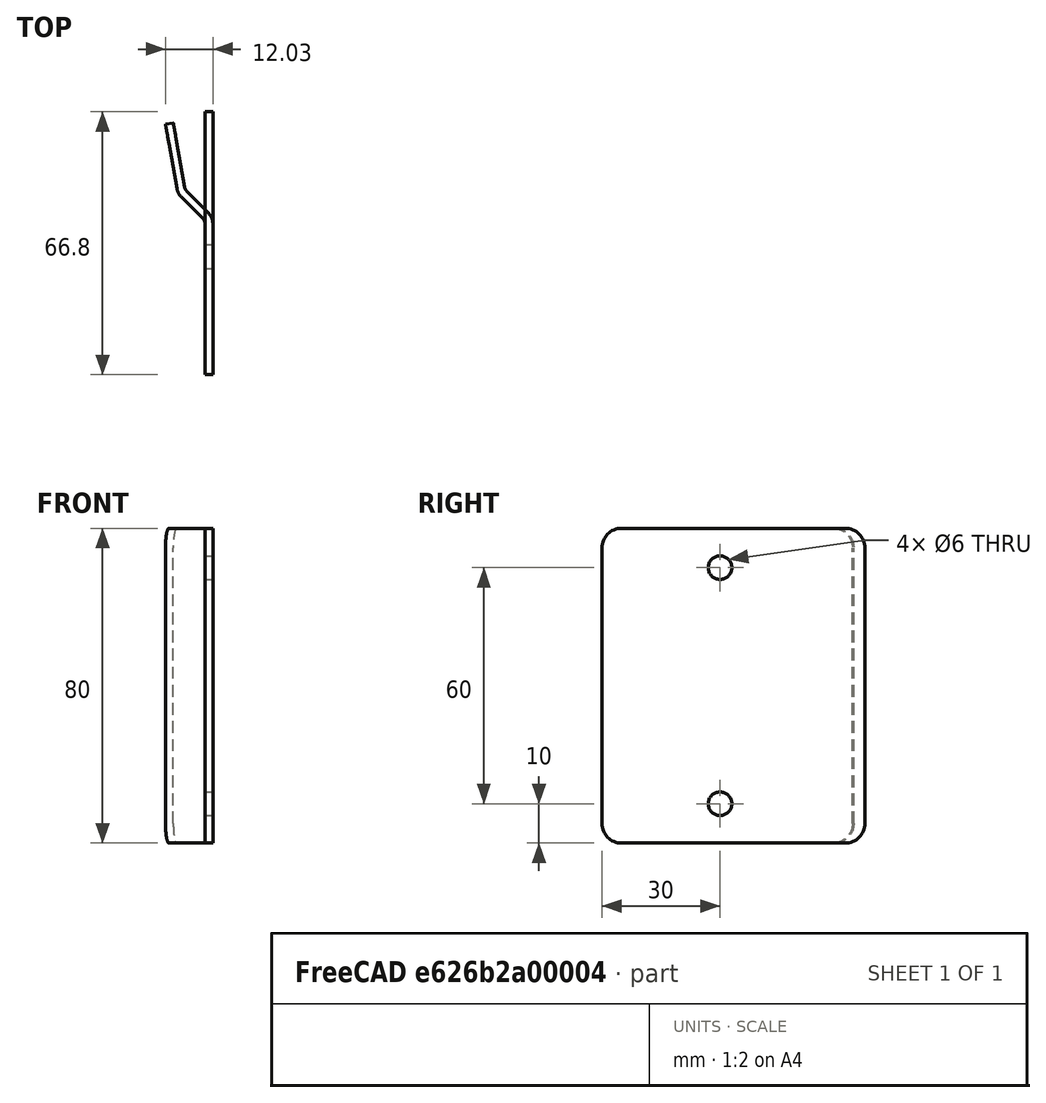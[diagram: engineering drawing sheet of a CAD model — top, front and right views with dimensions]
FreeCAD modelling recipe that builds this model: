
FCSTD DOCUMENT  (FreeCAD 0.22R37100 (Git))
Label: wall_mounted_stand_fix
License: All rights reserved
LicenseURL: http://en.wikipedia.org/wiki/All_rights_reserved
objects: Sketcher::SketchObject×8, TechDraw::DrawViewDimension×8, PartDesign::Pocket×3, TechDraw::DrawViewPart×3, App::DocumentObjectGroup×2, PartDesign::SubShapeBinder×1, PartDesign::FeaturePython×1, PartDesign::Mirrored×1, PartDesign::Body×1, TechDraw::DrawSVGTemplate×1, Part::Feature×1, TechDraw::DrawPage×1
note: 35 computed .brp shape members not serialized (recipe doc carries the construction recipe); baked Part::Feature solids carry a one-line shape summary decoded from their .brp

FEATURE [Sketcher::SketchObject] Sketch
  FullyConstrained = true
  sketch-geometry (3):
    g0: LineSegment StartX=0 StartY=0 StartZ=0 EndX=0 EndY=40 EndZ=0
    g1: LineSegment StartX=0 StartY=40 StartZ=0 EndX=-7.07107 EndY=47.0711 EndZ=0
    g2: LineSegment StartX=-7.07107 StartY=47.0711 StartZ=0 EndX=-10.0561 EndY=64 EndZ=0
  constraints (10):
    c: Coincident(g-1,g0)
    c: PointOnObject(g0,g-2)
    c: Coincident(g0,g1)
    c: Coincident(g1,g2)
    c: Angle(g1,g0) = 2.35619
    c: Angle(g1,g2) = 2.53073
    c: DistanceY(g0,g0) = 40
    c: Distance(g1) = 10
    c: Distance(g2) = 17.1901
    c: DistanceY(g0,g2) = 24
FEATURE [PartDesign::SubShapeBinder] Binder
  BindCopyOnChange = 0
  BindMode = 0
  ClaimChildren = true
  Context = -> Body [Binder.]
  Fuse = false
  MakeFace = true
  OffsetFill = false
  OffsetIntersection = false
  OffsetJoinType = 0
  OffsetOpenResult = false
  PartialLoad = false
  Relative = false
  Support = -> [Sketch]
  _Version = 2
FEATURE [PartDesign::FeaturePython] BaseBend  # WARN: FeaturePython — macro-defined, semantics opaque (R4)
  BendSide = 1
  BendSketch = -> Binder
  MidPlane = true
  Reverse = false
  Suppressed = false
  length = 80
  radius = 2
  thickness = 2
FEATURE [Sketcher::SketchObject] Sketch001
  AttachmentSupport = -> [YZ_Plane]
  FullyConstrained = true
  MapMode = 5
  Placement = pos=(0,0,0) rot=(0.57735,0.57735,0.57735;2.0944rad)
  sketch-geometry (2):
    g0: Circle CenterX=30 CenterY=30 CenterZ=0 NormalX=0 NormalY=0 NormalZ=1 AngleXU=0 Radius=3
    g1: Circle CenterX=30 CenterY=-30 CenterZ=0 NormalX=0 NormalY=0 NormalZ=1 AngleXU=0 Radius=3
  constraints (5):
    c: Symmetric(g1,g0,g-1)
    c: Equal(g0,g1)
    c: Diameter(g0) = 6
    c: DistanceX(g0) = 30
    c: DistanceY(g0) = 30
FEATURE [PartDesign::Pocket] Pocket
  BaseFeature = -> BaseBend
  Direction = (-1,0,0)
  Length = 5
  Length2 = 5
  Midplane = true
  Profile = -> Sketch001
  ReferenceAxis = -> Sketch001 [N_Axis]
  Suppressed = false
  Type = 1
FEATURE [Sketcher::SketchObject] Sketch003
  AttachmentOffset = pos=(0,40,0) rot=(0,0,1;0rad)
  AttachmentSupport = -> [YZ_Plane]
  FullyConstrained = true
  MapMode = 5
  Placement = pos=(0,0,40) rot=(0.57735,0.57735,0.57735;2.0944rad)
  expr: .AttachmentOffset.Base.y = <<BaseBend>>.length / 2
  sketch-geometry (3):
    g0: ArcOfCircle CenterX=5 CenterY=-5 CenterZ=0 NormalX=0 NormalY=0 NormalZ=1 AngleXU=0 Radius=5 StartAngle=1.5708 EndAngle=3.14159
    g1: LineSegment StartX=0 StartY=-5 StartZ=0 EndX=0 EndY=0 EndZ=0
    g2: LineSegment StartX=0 StartY=0 StartZ=0 EndX=5 EndY=0 EndZ=0
  constraints (7):
    c: Tangent(g0,g-1) = 1.5708
    c: Tangent(g0,g-2) = 1.5708
    c: Coincident(g0,g1)
    c: Coincident(g1,g2)
    c: Radius(g0) = 5
    c: Coincident(g2,g0)
    c: Coincident(g1,g-1)
FEATURE [Sketcher::SketchObject] Sketch004
  AttachmentOffset = pos=(0,40,0) rot=(0,-1,0;1.5708rad)
  AttachmentSupport = -> [Binder]
  FullyConstrained = true
  MapMode = 7
  Placement = pos=(-10.0561,64,40) rot=(0.6444,-0.540716,-0.540716;1.99673rad)
  expr: .AttachmentOffset.Base.y = <<BaseBend>>.length / 2
  sketch-geometry (3):
    g0: LineSegment StartX=3.14895e-11 StartY=-3.14335e-11 StartZ=0 EndX=5.00002 EndY=-3.14335e-11 EndZ=0
    g1: LineSegment StartX=3.14895e-11 StartY=-5.00002 StartZ=0 EndX=3.14895e-11 EndY=-3.14335e-11 EndZ=0
    g2: ArcOfCircle CenterX=5 CenterY=-5 CenterZ=0 NormalX=0 NormalY=0 NormalZ=1 AngleXU=0 Radius=5 StartAngle=1.57079 EndAngle=3.1416
  constraints (9):
    c: Coincident(g1,g0)
    c: Horizontal(g0)
    c: Vertical(g1)
    c: Coincident(g0,g-1)
    c: Coincident(g2,g0)
    c: Coincident(g2,g1)
    c: Tangent(g2,g-2)
    c: Tangent(g2,g-1)
    c: Radius(g2) = 5
FEATURE [PartDesign::Pocket] Pocket001
  BaseFeature = -> Pocket
  Direction = (0.984808,0.173648,0)
  Length = 5
  Length2 = 5
  Midplane = true
  Profile = -> Sketch004
  ReferenceAxis = -> Sketch004 [N_Axis]
  Suppressed = false
  Type = 1
FEATURE [PartDesign::Pocket] Pocket002
  BaseFeature = -> Pocket001
  Direction = (-1,0,0)
  Length = 5
  Length2 = 5
  Midplane = true
  Profile = -> Sketch003
  ReferenceAxis = -> Sketch003 [N_Axis]
  Suppressed = false
  Type = 1
FEATURE [PartDesign::Mirrored] Mirrored
  BaseFeature = -> Pocket002
  MirrorPlane = -> XY_Plane
  Originals = -> [Pocket001,Pocket002]
  Suppressed = false
FEATURE [PartDesign::Body] Body  label="wall_mounted_stand_fix"
  Group = -> [Binder,BaseBend,Sketch001,Pocket,Sketch003,Sketch004,Pocket001,Pocket002,Mirrored]
  Origin = -> Origin
  Tip = -> Mirrored
FEATURE [App::DocumentObjectGroup] Group  label="parts"
  Group = -> [Body]
FEATURE [TechDraw::DrawSVGTemplate] Template
  Height = 210
  Orientation = 1
  Template = <path>
  Width = 297
FEATURE [TechDraw::DrawViewPart] View002
  CoarseView = false
  Direction = (-1,0,0)
  Focus = 100
  HardHidden = false
  IsoCount = 0
  IsoHidden = false
  IsoVisible = false
  LockPosition = false
  Perspective = false
  Rotation = 0
  ScaleType = 0
  ScrubCount = 0
  SeamHidden = false
  SeamVisible = true
  SmoothHidden = false
  SmoothVisible = true
  Source = -> [Body]
  X = 58.5
  XDirection = (0,0,1)
  Y = 155
FEATURE [TechDraw::DrawViewPart] View
  CoarseView = false
  Direction = (0,0,1)
  Focus = 100
  HardHidden = false
  IsoCount = 0
  IsoHidden = false
  IsoVisible = false
  LockPosition = false
  Perspective = false
  Rotation = 0
  Scale = 2.5
  ScaleType = 2
  ScrubCount = 0
  SeamHidden = false
  SeamVisible = true
  SmoothHidden = false
  SmoothVisible = true
  Source = -> [Body]
  X = 198.5
  XDirection = (0,1,0)
  Y = 105
FEATURE [TechDraw::DrawViewPart] View003
  CoarseView = false
  Direction = (-0.57735,-0.57735,0.57735)
  Focus = 100
  HardHidden = false
  IsoCount = 0
  IsoHidden = false
  IsoVisible = false
  LockPosition = false
  Perspective = false
  Rotation = 0
  ScaleType = 0
  ScrubCount = 0
  SeamHidden = false
  SeamVisible = true
  SmoothHidden = false
  SmoothVisible = true
  Source = -> [Body]
  X = 58.5
  XDirection = (0,0.707107,0.707107)
  Y = 53
FEATURE [TechDraw::DrawViewDimension] Dimension
  AngleOverride = false
  Arbitrary = false
  ArbitraryTolerances = false
  BoxCorners = (2) [(-80,-15.0321,-1e-07),(80,15.0321,1e-07)]
  EqualTolerance = true
  ExtensionAngle = 0
  FormatSpec = %.2w
  FormatSpecOverTolerance = %+.2w
  FormatSpecUnderTolerance = %+.2w
  Inverted = false
  LineAngle = 0
  LockPosition = false
  MeasureType = 1
  OverTolerance = 0
  References2D = -> [View]
  Rotation = 0
  ScaleType = 0
  TheoreticalExact = false
  Type = 0
  UnderTolerance = 0
  X = 49.3248
  Y = 41.7301
FEATURE [TechDraw::DrawViewDimension] Dimension001
  AngleOverride = false
  Arbitrary = false
  ArbitraryTolerances = false
  BoxCorners = (2) [(-80,-15.0321,-1e-07),(80,15.0321,1e-07)]
  EqualTolerance = true
  ExtensionAngle = 0
  FormatSpec = %.2w
  FormatSpecOverTolerance = %+.2w
  FormatSpecUnderTolerance = %+.2w
  Inverted = false
  LineAngle = 0
  LockPosition = false
  MeasureType = 1
  OverTolerance = 0
  References2D = -> [View]
  Rotation = 0
  ScaleType = 0
  TheoreticalExact = false
  Type = 0
  UnderTolerance = 0
  X = 47.2724
  Y = -22.1268
FEATURE [TechDraw::DrawViewDimension] Dimension002
  AngleOverride = false
  Arbitrary = false
  ArbitraryTolerances = false
  BoxCorners = (2) [(-80,-15.0321,-1e-07),(80,15.0321,1e-07)]
  EqualTolerance = true
  ExtensionAngle = 0
  FormatSpec = %.2w
  FormatSpecOverTolerance = %+.2w
  FormatSpecUnderTolerance = %+.2w
  Inverted = false
  LineAngle = 0
  LockPosition = false
  MeasureType = 1
  OverTolerance = 0
  References2D = -> [View]
  Rotation = 0
  ScaleType = 0
  TheoreticalExact = false
  Type = 0
  UnderTolerance = 0
  X = -30.6032
  Y = -16.3526
FEATURE [TechDraw::DrawViewDimension] Dimension003
  AngleOverride = false
  Arbitrary = false
  ArbitraryTolerances = false
  BoxCorners = (2) [(-80,-15.0321,-1e-07),(80,15.0321,1e-07)]
  EqualTolerance = true
  ExtensionAngle = 0
  FormatSpec = %.2w
  FormatSpecOverTolerance = %+.2w
  FormatSpecUnderTolerance = %+.2w
  Inverted = false
  LineAngle = 0
  LockPosition = false
  MeasureType = 1
  OverTolerance = 0
  References2D = -> [View]
  Rotation = 0
  ScaleType = 0
  TheoreticalExact = false
  Type = 6
  UnderTolerance = 0
  X = 17.6962
  Y = 10.8724
FEATURE [TechDraw::DrawViewDimension] Dimension004
  AngleOverride = false
  Arbitrary = false
  ArbitraryTolerances = false
  BoxCorners = (2) [(-80,-15.0321,-1e-07),(80,15.0321,1e-07)]
  EqualTolerance = true
  ExtensionAngle = 0
  FormatSpec = %.2w
  FormatSpecOverTolerance = %+.2w
  FormatSpecUnderTolerance = %+.2w
  Inverted = false
  LineAngle = 0
  LockPosition = false
  MeasureType = 1
  OverTolerance = 0
  References2D = -> [View]
  Rotation = 0
  ScaleType = 0
  TheoreticalExact = false
  Type = 6
  UnderTolerance = 0
  X = 36.6095
  Y = -11.2103
FEATURE [TechDraw::DrawViewDimension] Dimension005  label="Dimension3D005"
  AngleOverride = true
  Arbitrary = true
  ArbitraryTolerances = false
  BoxCorners = (2) [(-48.8486,-32.9544,-1e-07),(48.8486,32.9544,1e-07)]
  EqualTolerance = true
  ExtensionAngle = 150
  FormatSpec = 40
  FormatSpecOverTolerance = %+.2w
  FormatSpecUnderTolerance = %+.2w
  Inverted = false
  LineAngle = 30
  LockPosition = false
  MeasureType = 1
  OverTolerance = 0
  References2D = -> [View003]
  Rotation = 0
  ScaleType = 0
  TheoreticalExact = false
  Type = 0
  UnderTolerance = 0
  X = 26.2269
  Y = -30.6564
FEATURE [TechDraw::DrawViewDimension] Dimension006
  AngleOverride = true
  Arbitrary = false
  ArbitraryTolerances = false
  BoxCorners = (2) [(-48.8486,-32.9544,-1e-07),(48.8486,32.9544,1e-07)]
  EqualTolerance = true
  ExtensionAngle = 150
  FormatSpec = %.2w
  FormatSpecOverTolerance = %+.2w
  FormatSpecUnderTolerance = %+.2w
  Inverted = false
  LineAngle = 60
  LockPosition = false
  MeasureType = 1
  OverTolerance = 0
  References2D = -> [View003]
  Rotation = 0
  ScaleType = 0
  TheoreticalExact = false
  Type = 0
  UnderTolerance = 0
  X = 42.5219
  Y = -11.533
FEATURE [Part::Feature] Unfold
  shape: bbox 2.002 x 66.81 x 80 mm, 12 faces (baked)
FEATURE [Sketcher::SketchObject] Unfold_Sketch
  FullyConstrained = false
  sketch-geometry (10):
    g0: LineSegment StartX=40 StartY=-5 StartZ=0 EndX=40 EndY=-61.804 EndZ=0
    g1: ArcOfCircle CenterX=35 CenterY=-5 CenterZ=0 NormalX=0 NormalY=0 NormalZ=1 AngleXU=-1.5708 Radius=5 StartAngle=1.5708 EndAngle=3.14159
    g2: LineSegment StartX=35 StartY=0 StartZ=0 EndX=-35 EndY=0 EndZ=0
    g3: ArcOfCircle CenterX=-35 CenterY=-5 CenterZ=0 NormalX=0 NormalY=0 NormalZ=1 AngleXU=-1.5708 Radius=5 StartAngle=3.14159 EndAngle=4.71239
    g4: LineSegment StartX=-40 StartY=-5 StartZ=0 EndX=-40 EndY=-61.804 EndZ=0
    g5: ArcOfCircle CenterX=-35 CenterY=-61.804 CenterZ=0 NormalX=0 NormalY=0 NormalZ=1 AngleXU=1.5708 Radius=5 StartAngle=1.57079 EndAngle=3.1416
    g6: LineSegment StartX=35 StartY=-66.804 StartZ=0 EndX=-35 EndY=-66.804 EndZ=0
    g7: ArcOfCircle CenterX=35 CenterY=-61.804 CenterZ=0 NormalX=0 NormalY=0 NormalZ=1 AngleXU=1.5708 Radius=5 StartAngle=3.14159 EndAngle=4.71239
    g8: Circle CenterX=-30 CenterY=-30 CenterZ=0 NormalX=0 NormalY=0 NormalZ=-1 AngleXU=-1.5708 Radius=3
    g9: Circle CenterX=30 CenterY=-30 CenterZ=0 NormalX=0 NormalY=0 NormalZ=-1 AngleXU=-1.5708 Radius=3
FEATURE [Sketcher::SketchObject] Unfold_Sketch_Outline
  FullyConstrained = false
  sketch-geometry (8):
    g0: LineSegment StartX=40 StartY=-5 StartZ=0 EndX=40 EndY=-61.804 EndZ=0
    g1: ArcOfCircle CenterX=35 CenterY=-61.804 CenterZ=0 NormalX=0 NormalY=0 NormalZ=1 AngleXU=1.5708 Radius=5 StartAngle=3.14159 EndAngle=4.71239
    g2: LineSegment StartX=35 StartY=-66.804 StartZ=0 EndX=-35 EndY=-66.804 EndZ=0
    g3: ArcOfCircle CenterX=-35 CenterY=-61.804 CenterZ=0 NormalX=0 NormalY=0 NormalZ=1 AngleXU=1.5708 Radius=5 StartAngle=1.57079 EndAngle=3.1416
    g4: LineSegment StartX=-40 StartY=-5 StartZ=0 EndX=-40 EndY=-61.804 EndZ=0
    g5: ArcOfCircle CenterX=-35 CenterY=-5 CenterZ=0 NormalX=0 NormalY=0 NormalZ=1 AngleXU=-1.5708 Radius=5 StartAngle=3.14159 EndAngle=4.71239
    g6: LineSegment StartX=35 StartY=0 StartZ=0 EndX=-35 EndY=0 EndZ=0
    g7: ArcOfCircle CenterX=35 CenterY=-5 CenterZ=0 NormalX=0 NormalY=0 NormalZ=1 AngleXU=-1.5708 Radius=5 StartAngle=1.5708 EndAngle=3.14159
FEATURE [Sketcher::SketchObject] Unfold_Sketch_Internal
  FullyConstrained = false
  sketch-geometry (2):
    g0: Circle CenterX=30 CenterY=-30 CenterZ=0 NormalX=0 NormalY=0 NormalZ=-1 AngleXU=-1.5708 Radius=3
    g1: Circle CenterX=-30 CenterY=-30 CenterZ=0 NormalX=0 NormalY=0 NormalZ=-1 AngleXU=-1.5708 Radius=3
FEATURE [Sketcher::SketchObject] Unfold_Sketch_bends
  FullyConstrained = false
  sketch-geometry (2):
    g0: LineSegment StartX=-40 StartY=-49.3282 StartZ=0 EndX=40 EndY=-49.3282 EndZ=0
    g1: LineSegment StartX=-40 StartY=-39.5212 StartZ=0 EndX=40 EndY=-39.5212 EndZ=0
FEATURE [TechDraw::DrawViewDimension] Dimension007
  AngleOverride = false
  Arbitrary = false
  ArbitraryTolerances = false
  BoxCorners = (2) [(-40,-32,-1e-07),(40,32,1e-07)]
  EqualTolerance = true
  ExtensionAngle = 0
  FormatSpec = %.2w
  FormatSpecOverTolerance = %+.2w
  FormatSpecUnderTolerance = %+.2w
  Inverted = false
  LineAngle = 0
  LockPosition = false
  MeasureType = 1
  OverTolerance = 0
  References2D = -> [View002]
  Rotation = 0
  ScaleType = 0
  TheoreticalExact = false
  Type = 1
  UnderTolerance = 0
  X = 0
  Y = 0.5
FEATURE [TechDraw::DrawPage] Page
  KeepUpdated = true
  NextBalloonIndex = 1
  ProjectionType = 0
  Template = -> Template
  Views = -> [View002,View,View003,Dimension,Dimension001,Dimension002,Dimension003,Dimension004,Dimension005,Dimension006,Dimension007]
FEATURE [App::DocumentObjectGroup] Group001  label="unfolds"
  Group = -> [Page,Unfold,Unfold_Sketch,Unfold_Sketch_Outline,Unfold_Sketch_Internal,Unfold_Sketch_bends]
note: 1 file-system path scrubbed to <path> (originals preserved in the JSON sidecar)
